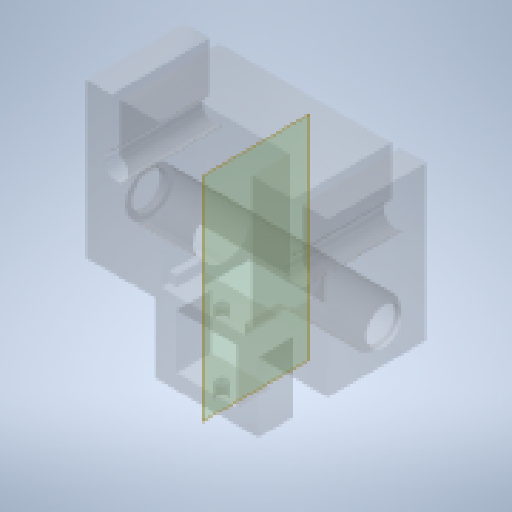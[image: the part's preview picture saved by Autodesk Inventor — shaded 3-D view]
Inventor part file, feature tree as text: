
AUTODESK INVENTOR PART (.ipt)
format: ipt  version: 2023 (Build 270158000, 158)  size: 596,480 bytes
history: native  units: mm
features: extrude x18, sketch x18, projected_geometry x7, plane x1
ambient origin geometry x8: Origin, YZ Plane, XZ Plane, XY Plane, X Axis, Y Axis, Z Axis, Center Point
bodies: Solid1 (feature_tree)
feature tree (44):
  extrude  "Extrusion1"  Depth=10.0mm
  extrude  "Extrusion5"  Depth=1.5mm
  extrude  "Extrusion11"  Depth=10.0mm
  extrude  "Extrusion13"  Depth=80.0mm
  extrude  "Extrusion14"  TaperAngle=0.0deg  [1 undecoded]
  extrude  "Extrusion15"  Depth=20.0mm
  extrude  "Extrusion16"  Depth=20.0mm
  extrude  "Extrusion17"  Depth=10.0mm
  extrude  "Extrusion18"  Depth=20.0mm
  plane  "Work Plane5"
  extrude  "Extrusion21"  Depth=35.0mm
  extrude  "Extrusion19"  Depth=80.0mm TaperAngle=0.0deg
  extrude  "Extrusion20"  Depth=1.0mm TaperAngle=0.0deg
  extrude  "Extrusion22"  Depth=5.0mm
  extrude  "Extrusion23"  Depth=6.0mm TaperAngle=0.0deg
  extrude  "Extrusion24"  Depth=30.0mm
  extrude  "Extrusion25"  Depth=15.0mm
  extrude  "Extrusion26"  Depth=37.0mm TaperAngle=0.0deg
  extrude  "Extrusion27"  Depth=7.0mm
  sketch  "Sketch1"  dims[d2=8.0mm d3=10.0mm]
  sketch  "Sketch5"  dims[d7=1.5mm d8=1.5mm]
  sketch  "Sketch13"  dims[d9=36.0mm d10=0.0mm d16=10.0mm]
  projected_geometry  "Projected Loop1"
  sketch  "Sketch16"  dims[d17=8.0mm d18=1.5mm d19=1.5mm d20=10.0mm d21=8.0mm d22=80.0mm]
  sketch  "Sketch17"  dims[d23=10.0mm d24=0.0mm]
  sketch  "Sketch18"  dims[d25=60.0mm d26=20.0mm]
  sketch  "Sketch19"  dims[d27=20.0mm d28=20.0mm]
  sketch  "Sketch20"  dims[d29=20.0mm d30=10.0mm]
  sketch  "Sketch21"  dims[d31=10.0mm d32=20.0mm]
  projected_geometry  "Projected Loop2"
  sketch  "Sketch22"  dims[d40=30.0mm d41=35.0mm]
  sketch  "Sketch24"  dims[d45=20.0mm d46=80.0mm d47=0.0mm]
  sketch  "Sketch25"  dims[d79=25.0mm d82=25.0mm d83=1.0mm d84=0.0mm]
  sketch  "Sketch26"  dims[d85=15.0mm d86=5.0mm]
  projected_geometry  "Projected Loop3"
  sketch  "Sketch27"  dims[d87=15.0mm d103=6.0mm d104=0.0mm]
  projected_geometry  "Projected Loop4"
  sketch  "Sketch28"  dims[d105=20.0mm d106=0.0mm d107=30.0mm]
  sketch  "Sketch29"  dims[d108=25.0mm d109=15.0mm]
  sketch  "Sketch30"  dims[d110=0.0mm d111=37.0mm d112=0.0mm]
  projected_geometry  "Projected Loop5"
  projected_geometry  "Projected Loop6"
  projected_geometry  "Projected Loop7"
  sketch  "Sketch31"  dims[d113=7.0mm d114=7.0mm d115=5.0mm d116=18.0mm d117=20.0mm d118=23.0mm d119=15.5mm d120=0.0mm d121=3.5mm d122=7.5mm d123=40.0mm d124=80.0mm d125=0.0mm d126=2.5mm d127=0.0mm d128=15.0mm d129=8.0mm d130=8.0mm d131=75.0mm d132=0.0mm d133=25.0mm d134=27.5mm d135=15.0mm d136=10.0mm d137=0.0mm d138=27.5mm d139=27.5mm d140=30.0mm d141=7.5mm d142=0.0mm d143=12.0mm d144=2.5mm d145=0.0mm d146=2.5mm d147=0.0mm d148=0.5mm d149=0.5mm d150=30.5mm d151=0.0mm d152=1.5mm d153=100.5mm d154=0.0mm d155=15.0mm d156=0.0mm d157=20.0mm d158=20.0mm d159=15.0mm d160=0.0mm]
note: 1 required parameter value undecoded (feature->parameter linkage not recoverable at this tier; creation-order binding heuristic only, values carry confidence <= 0.55)
